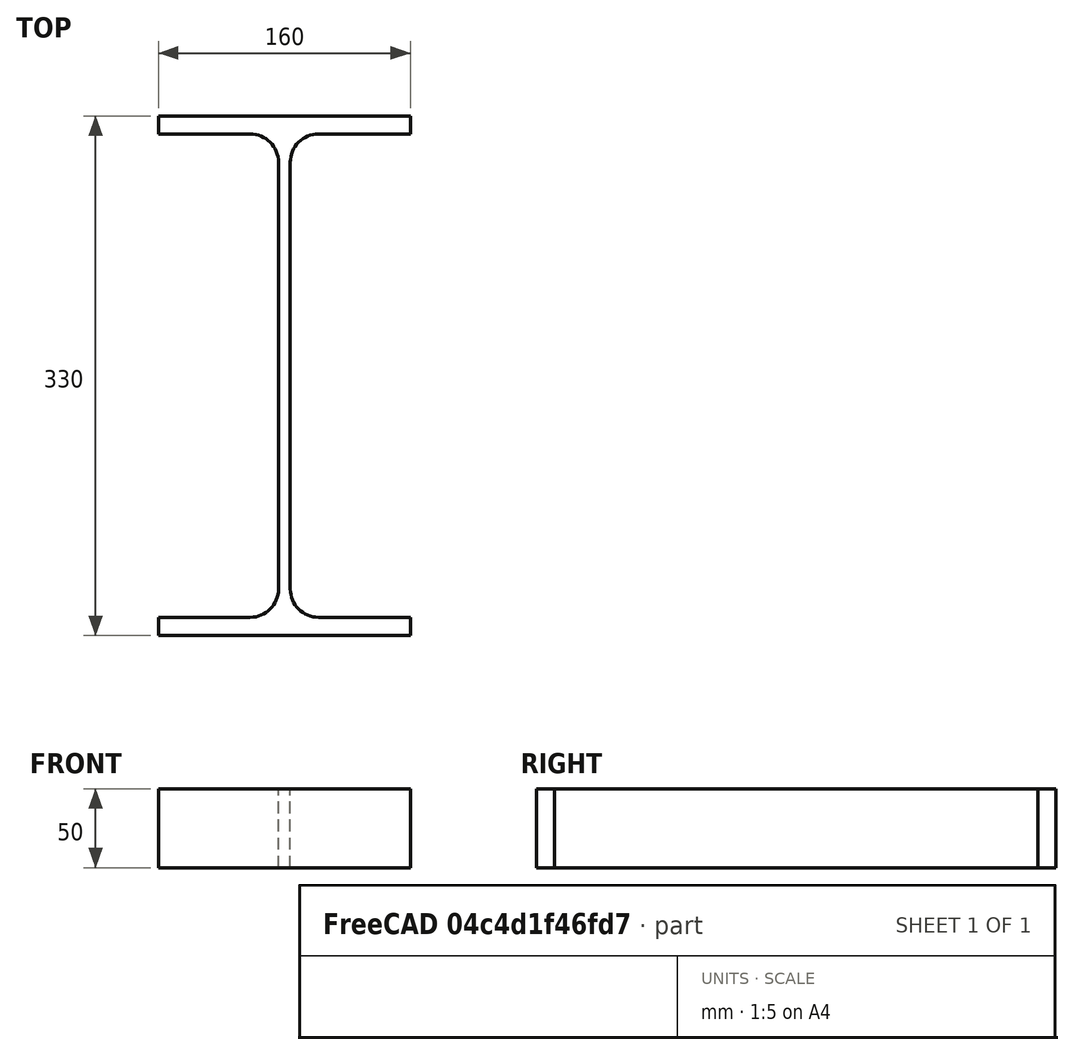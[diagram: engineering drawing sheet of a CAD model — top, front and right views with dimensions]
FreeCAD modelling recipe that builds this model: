
FCSTD DOCUMENT  (FreeCAD 0.15R4671 (Git))
Label: IPE-Profile 330 DIN1025-5 S235JR
License: All rights reserved
LicenseURL: http://en.wikipedia.org/wiki/All_rights_reserved
objects: Sketcher::SketchObject×1, Part::Extrusion×1
note: 2 computed .brp shape members not serialized (recipe doc carries the construction recipe); baked Part::Feature solids carry a one-line shape summary decoded from their .brp

FEATURE [Sketcher::SketchObject] Sketch
  sketch-geometry (16):
    g0: LineSegment StartX=3.75 StartY=-135.5 StartZ=0 EndX=3.75 EndY=135.5 EndZ=0
    g1: LineSegment StartX=21.75 StartY=153.5 StartZ=0 EndX=80 EndY=153.5 EndZ=0
    g2: LineSegment StartX=80 StartY=153.5 StartZ=0 EndX=80 EndY=165 EndZ=0
    g3: LineSegment StartX=80 StartY=165 StartZ=0 EndX=-80 EndY=165 EndZ=0
    g4: LineSegment StartX=-80 StartY=165 StartZ=0 EndX=-80 EndY=153.5 EndZ=0
    g5: LineSegment StartX=-80 StartY=153.5 StartZ=0 EndX=-21.75 EndY=153.5 EndZ=0
    g6: LineSegment StartX=-3.75 StartY=135.5 StartZ=0 EndX=-3.75 EndY=-135.5 EndZ=0
    g7: LineSegment StartX=-21.75 StartY=-153.5 StartZ=0 EndX=-80 EndY=-153.5 EndZ=0
    g8: LineSegment StartX=-80 StartY=-153.5 StartZ=0 EndX=-80 EndY=-165 EndZ=0
    g9: LineSegment StartX=-80 StartY=-165 StartZ=0 EndX=80 EndY=-165 EndZ=0
    g10: LineSegment StartX=80 StartY=-165 StartZ=0 EndX=80 EndY=-153.5 EndZ=0
    g11: LineSegment StartX=80 StartY=-153.5 StartZ=0 EndX=21.75 EndY=-153.5 EndZ=0
    g12: ArcOfCircle CenterX=21.75 CenterY=135.5 CenterZ=0 NormalX=0 NormalY=0 NormalZ=1 Radius=18 StartAngle=1.5708 EndAngle=3.14159
    g13: ArcOfCircle CenterX=21.75 CenterY=-135.5 CenterZ=0 NormalX=0 NormalY=0 NormalZ=1 Radius=18 StartAngle=3.14159 EndAngle=4.71239
    g14: ArcOfCircle CenterX=-21.75 CenterY=135.5 CenterZ=0 NormalX=0 NormalY=0 NormalZ=1 Radius=18 StartAngle=0 EndAngle=1.5708
    g15: ArcOfCircle CenterX=-21.75 CenterY=-135.5 CenterZ=0 NormalX=0 NormalY=0 NormalZ=1 Radius=18 StartAngle=4.71239 EndAngle=6.28319
  constraints (42):
    c: Vertical(g0)
    c: Coincident(g2,g1)
    c: Vertical(g2)
    c: Coincident(g3,g2)
    c: Coincident(g4,g3)
    c: Vertical(g4)
    c: Coincident(g5,g4)
    c: Horizontal(g5)
    c: Vertical(g6)
    c: Horizontal(g7)
    c: Coincident(g8,g7)
    c: Vertical(g8)
    c: Coincident(g9,g8)
    c: Horizontal(g9)
    c: Coincident(g10,g9)
    c: Vertical(g10)
    c: Coincident(g11,g10)
    c: Horizontal(g11)
    c: Tangent(g1,g12) = 1.5708
    c: Tangent(g0,g12) = 1.5708
    c: Tangent(g0,g13) = 1.5708
    c: Tangent(g11,g13) = 1.5708
    c: Tangent(g5,g14) = 1.5708
    c: Tangent(g6,g14) = 1.5708
    c: Tangent(g6,g15) = 1.5708
    c: Tangent(g7,g15) = 1.5708
    c: Equal(g3,g9)
    c: Equal(g2,g4)
    c: Equal(g4,g8)
    c: Equal(g8,g10)
    c: Equal(g12,g14)
    c: Equal(g14,g15)
    c: Equal(g15,g13)
    c: Symmetric(g2,g3,g-2)
    c: Symmetric(g9,g8,g-2)
    c: Symmetric(g0,g6,g-2)
    c: Symmetric(g2,g9,g-1)
    c: DistanceY(g2,g9) = -330
    c: DistanceX(g3) = -160
    c: DistanceX(g0,g6) = -7.5
    c: DistanceY(g2) = 11.5
    c: Radius(g12) = 18
FEATURE [Part::Extrusion] Extrude  label="IPE-Profile 330 DIN1025-5 S235JR"
  Base = -> Sketch
  Dir = (0,0,50)
  Solid = true
